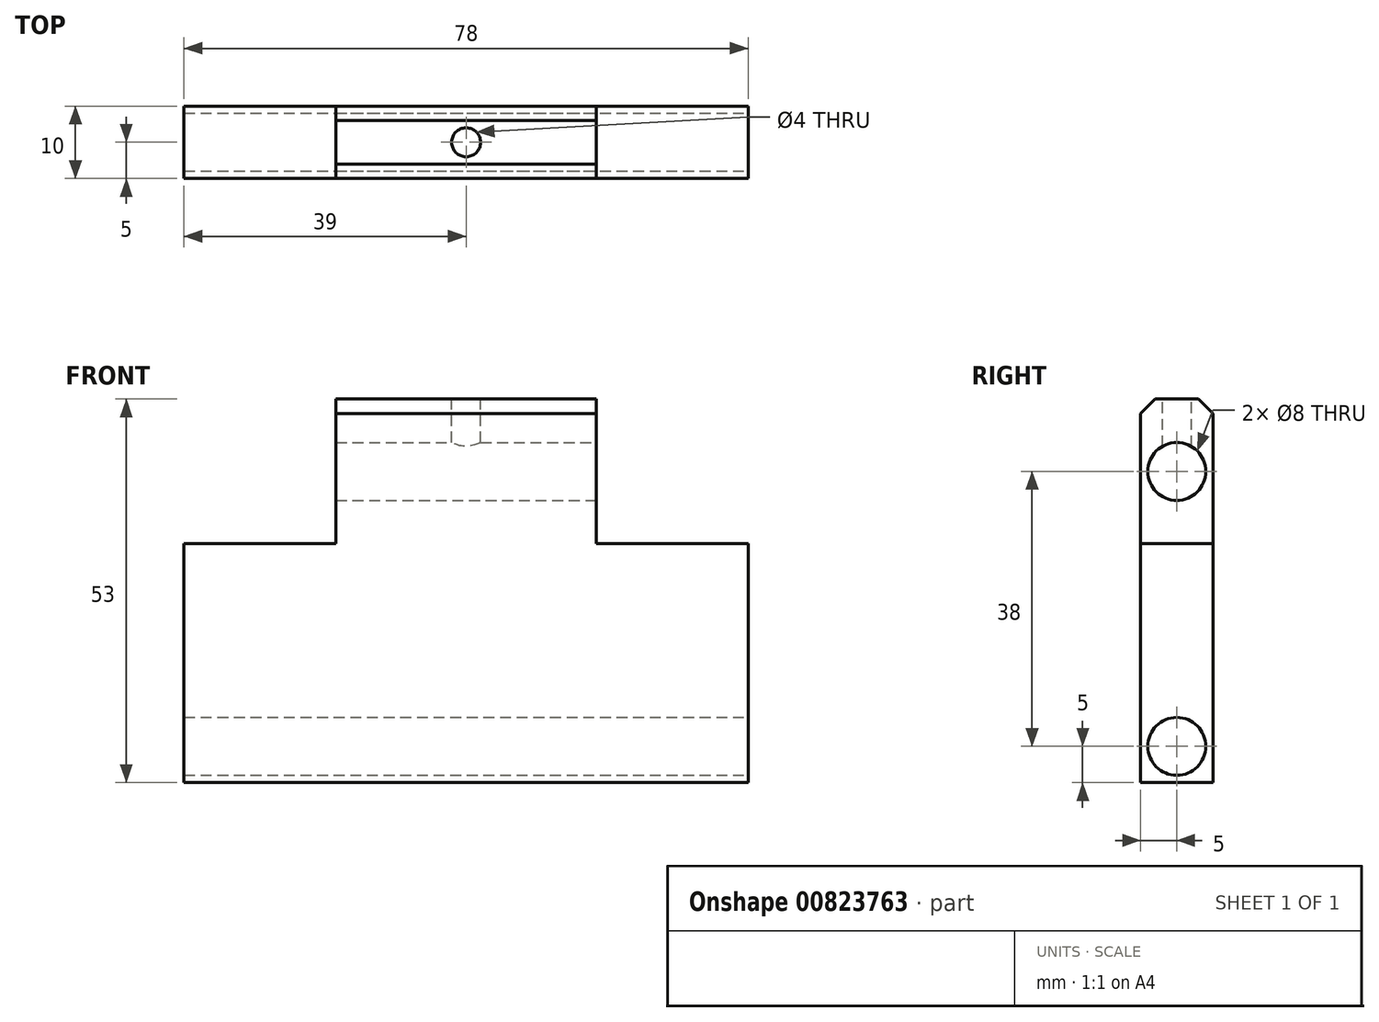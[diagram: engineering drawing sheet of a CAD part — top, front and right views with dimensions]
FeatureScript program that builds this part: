
annotation { "Feature Type Name" : "Feature", "Feature Type Description" : "" }
export const myFeature = defineFeature(function(context is Context, id is Id, definition is map)
    precondition{}
    {
        {
            var Q0;
            Q0=qCreatedBy(makeId("Front.planeOp"),FACE);
            var sketch = newSketch(context, id + "F0", { "sketchPlane" : qUnion([Q0])});
            skLineSegment(sketch, "E0.bottom", {"start": v(-19, 24) * mm, "end": v(19, 24) * mm});
            skLineSegment(sketch, "E0.top", {"start": v(-35, -24) * mm, "end": v(35, -24) * mm});
            skLineSegment(sketch, "E0.left", {"start": v(-35, 9) * mm, "end": v(-35, -24) * mm});
            skLineSegment(sketch, "E0.right", {"start": v(35, 9) * mm, "end": v(35, -24) * mm});
            skPoint(sketch, "E0.middle", {"position": v(0, 0) * mm});
            skLineSegment(sketch, "E1.left", {"start": v(19, 9) * mm, "end": v(19, 24) * mm});
            skLineSegment(sketch, "E1.right", {"start": v(-19, 9) * mm, "end": v(-19, 24) * mm});
            skPoint(sketch, "E1.middle", {"position": v(0, 24) * mm});
            skPoint(sketch, "E1.top.end.orphan", {"position": v(-19, 39) * mm});
            skPoint(sketch, "E2.orphan", {"position": v(19, 39) * mm});
            skLineSegment(sketch, "E3", {"start": v(-19, 9) * mm, "end": v(-35, 9) * mm});
            skLineSegment(sketch, "E4", {"start": v(-35, 9) * mm, "end": v(-19, 9) * mm});
            skPoint(sketch, "E5.orphan", {"position": v(-35, 24) * mm});
            skLineSegment(sketch, "E6", {"start": v(19, 9) * mm, "end": v(35, 9) * mm});
            skPoint(sketch, "E7.orphan", {"position": v(35, 24) * mm});
            skSolve(sketch);
        }
        {
            var Q0;
            Q0=makeQuery(id+"F0.imprint","IMPRINT",FACE,{"disambiguationData":[TD([[makeQuery(id+"F0.imprint","IMPRINT",EDGE,{"derivedFrom":sQuery(id+"F0.wireOp",EDGE,"E0.bottom")}),-1.0]])]});
            extrude(context, id + "F1", {"entities" : qUnion([Q0]), "depth" : 10 * mm, "offsetDistance" : 25 * mm});
        }
        {
            var Q0;
            Q0=makeQuery(id+"F1.opExtrude","SWEPT_FACE",FACE,{"disambiguationData":[OSD([sQuery(id+"F0.wireOp",EDGE,"E1.left")])]});
            var sketch = newSketch(context, id + "F2", { "sketchPlane" : qUnion([Q0])});
            skCircle(sketch, "E8", {"center": v(-5, 19) * mm, "radius": 4 * mm});
            skPoint(sketch, "E8.centerSnap0", {"position": v(-5, 24) * mm});
            skSolve(sketch);
        }
        {
            var Q0;
            Q0=qSketchRegion(id+"F2",true);
            extrude(context, id + "F3", {"entities" : qUnion([Q0]), "operationType" : NewBodyOperationType.REMOVE, "oppositeDirection" : true, "depth" : 38 * mm, "offsetDistance" : 25 * mm});
        }
        {
            var Q0;
            Q0=makeQuery(id+"F1.opExtrude","SWEPT_FACE",FACE,{"disambiguationData":[OSD([sQuery(id+"F0.wireOp",EDGE,"E0.right")])]});
            var sketch = newSketch(context, id + "F4", { "sketchPlane" : qUnion([Q0])});
            skCircle(sketch, "E9", {"center": v(-5, -19) * mm, "radius": 4 * mm});
            skPoint(sketch, "E9.centerSnap0", {"position": v(-5, -24) * mm});
            skSolve(sketch);
        }
        {
            var Q0;
            Q0=makeQuery(id+"F4.imprint","IMPRINT",FACE,{"disambiguationData":[TD([[makeQuery(id+"F4.imprint","IMPRINT",EDGE,{"derivedFrom":sQuery(id+"F4.wireOp",EDGE,"E9")}),1.0]])]});
            extrude(context, id + "F5", {"entities" : qUnion([Q0]), "operationType" : NewBodyOperationType.REMOVE, "oppositeDirection" : true, "depth" : 70 * mm, "offsetDistance" : 25 * mm});
        }
        {
            var Q0;
            Q0=makeQuery(id+"F1.opExtrude","SWEPT_BODY",BODY,{"disambiguationData":[OSD([sQuery(id+"F0.wireOp",EDGE,"E0.bottom"),sQuery(id+"F0.wireOp",EDGE,"E0.top"),sQuery(id+"F0.wireOp",EDGE,"E0.left"),sQuery(id+"F0.wireOp",EDGE,"E0.right"),sQuery(id+"F0.wireOp",EDGE,"E1.left"),sQuery(id+"F0.wireOp",EDGE,"E1.right"),sQuery(id+"F0.wireOp",EDGE,"E4"),sQuery(id+"F0.wireOp",EDGE,"E6")])]});
            deleteBodies(context, id + "F6", {"entities" : qUnion([Q0])});
        }
        {
            var Q0;
            Q0=qCreatedBy(makeId("Front.planeOp"),FACE);
            var sketch = newSketch(context, id + "F7", { "sketchPlane" : qUnion([Q0])});
            skLineSegment(sketch, "E10.bottom", {"start": v(-18, 24) * mm, "end": v(18, 24) * mm});
            skLineSegment(sketch, "E10.top", {"start": v(-39, -24) * mm, "end": v(39, -24) * mm});
            skLineSegment(sketch, "E10.left", {"start": v(-39, 9) * mm, "end": v(-39, -24) * mm});
            skLineSegment(sketch, "E10.right", {"start": v(39, 9) * mm, "end": v(39, -24) * mm});
            skPoint(sketch, "E10.middle", {"position": v(0, 0) * mm});
            skLineSegment(sketch, "E11.top", {"start": v(-39, 9) * mm, "end": v(-18, 9) * mm});
            skLineSegment(sketch, "E11.right", {"start": v(-18, 24) * mm, "end": v(-18, 9) * mm});
            skLineSegment(sketch, "E12.top", {"start": v(39, 9) * mm, "end": v(18, 9) * mm});
            skLineSegment(sketch, "E12.right", {"start": v(18, 24) * mm, "end": v(18, 9) * mm});
            skSolve(sketch);
        }
        {
            var Q0;
            Q0=qSketchRegion(id+"F7",true);
            var Q1;
            Q1=makeQuery(id+"F7.imprint","IMPRINT",FACE,{"disambiguationData":[TD([[makeQuery(id+"F7.imprint","IMPRINT",EDGE,{"derivedFrom":sQuery(id+"F7.wireOp",EDGE,"E10.bottom")}),-1.0]])]});
            extrude(context, id + "F8", {"entities" : qUnion([Q0, Q1]), "depth" : 10 * mm, "offsetDistance" : 25 * mm});
        }
        {
            var Q0;
            Q0=makeQuery(id+"F8.opExtrude","SWEPT_FACE",FACE,{"disambiguationData":[OSD([sQuery(id+"F7.wireOp",EDGE,"E12.right")])]});
            var sketch = newSketch(context, id + "F9", { "sketchPlane" : qUnion([Q0])});
            skCircle(sketch, "E13", {"center": v(-5, 19) * mm, "radius": 4 * mm});
            skPoint(sketch, "E13.centerSnap0", {"position": v(-5, 24) * mm});
            skSolve(sketch);
        }
        {
            var Q0;
            Q0=qSketchRegion(id+"F9",true);
            extrude(context, id + "F10", {"entities" : qUnion([Q0]), "operationType" : NewBodyOperationType.REMOVE, "oppositeDirection" : true, "depth" : 40 * mm, "offsetDistance" : 25 * mm});
        }
        {
            var Q0;
            Q0=makeQuery(id+"F8.opExtrude","SWEPT_FACE",FACE,{"disambiguationData":[OSD([sQuery(id+"F7.wireOp",EDGE,"E10.right")])]});
            var sketch = newSketch(context, id + "F11", { "sketchPlane" : qUnion([Q0])});
            skCircle(sketch, "E14", {"center": v(-5, -19) * mm, "radius": 4 * mm});
            skPoint(sketch, "E14.centerSnap0", {"position": v(-5, -24) * mm});
            skSolve(sketch);
        }
        {
            var Q0;
            Q0=qSketchRegion(id+"F11",true);
            extrude(context, id + "F12", {"entities" : qUnion([Q0]), "operationType" : NewBodyOperationType.REMOVE, "oppositeDirection" : true, "depth" : 100 * mm, "offsetDistance" : 25 * mm});
        }
        {
            var Q0;
            Q0=makeQuery(id+"F8.opExtrude","SWEPT_FACE",FACE,{"disambiguationData":[OSD([sQuery(id+"F7.wireOp",EDGE,"E10.bottom")])]});
            extrude(context, id + "F13", {"entities" : qUnion([Q0]), "operationType" : NewBodyOperationType.ADD, "depth" : 5 * mm, "offsetDistance" : 25 * mm});
        }
        {
            var Q0;
            Q0=makeQuery(id+"F13.opExtrude","CAP_FACE",FACE,{"disambiguationData":[OSD([sQuery(id+"F7.wireOp",EDGE,"E10.bottom")])],"isStart":false});
            var sketch = newSketch(context, id + "F14", { "sketchPlane" : qUnion([Q0])});
            skCircle(sketch, "E15", {"center": v(0, -5) * mm, "radius": 2 * mm});
            skPoint(sketch, "E15.centerSnap0", {"position": v(0, -10) * mm});
            skPoint(sketch, "E15.centerSnap1", {"position": v(-18, -5) * mm});
            skSolve(sketch);
        }
        {
            var Q0;
            Q0=makeQuery(id+"F14.imprint","IMPRINT",FACE,{"disambiguationData":[TD([[makeQuery(id+"F14.imprint","IMPRINT",EDGE,{"derivedFrom":sQuery(id+"F14.wireOp",EDGE,"E15")}),1.0]])]});
            extrude(context, id + "F15", {"entities" : qUnion([Q0]), "operationType" : NewBodyOperationType.REMOVE, "oppositeDirection" : true, "depth" : 10 * mm, "offsetDistance" : 25 * mm});
        }
        {
            var Q0;
            {var subQ0=sQuery(id+"F7.wireOp",EDGE,"E10.bottom");Q0=makeQuery(id+"F13.opExtrude","CAP_EDGE",EDGE,{"disambiguationData":[OSD([subQ0]),TDD([makeQuery(id+"F8.opExtrude","CAP_EDGE",EDGE,{"disambiguationData":[OSD([subQ0])],"isStart":false})])],"isStart":false});}
            var Q1;
            {var subQ0=sQuery(id+"F7.wireOp",EDGE,"E10.bottom");Q1=makeQuery(id+"F13.opExtrude","CAP_EDGE",EDGE,{"disambiguationData":[OSD([subQ0]),TDD([makeQuery(id+"F8.opExtrude","CAP_EDGE",EDGE,{"disambiguationData":[OSD([subQ0])],"isStart":true})])],"isStart":false});}
            chamfer(context, id + "F16", {"entities" : qUnion([Q0, Q1]), "width" : 2 * mm, "tangentPropagation" : true});
        }
    });
